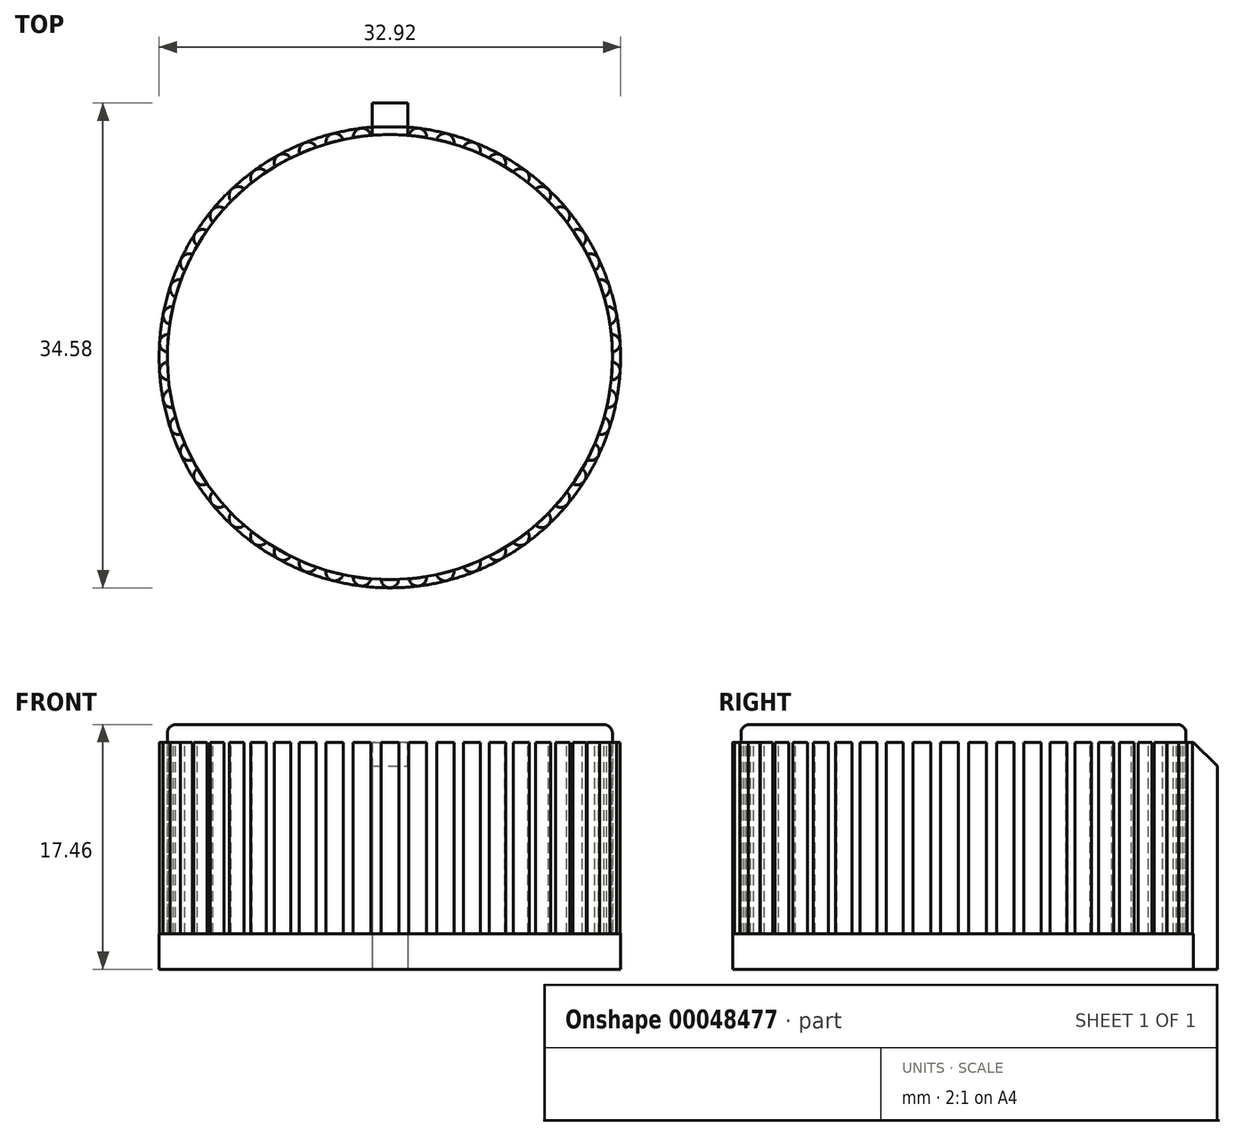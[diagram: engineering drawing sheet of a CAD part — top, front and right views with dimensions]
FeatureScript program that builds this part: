
annotation { "Feature Type Name" : "Feature", "Feature Type Description" : "" }
export const myFeature = defineFeature(function(context is Context, id is Id, definition is map)
    precondition{}
    {
        {
            var Q0;
            Q0=qCreatedBy(makeId("Top.planeOp"),FACE);
            var sketch = newSketch(context, id + "F0", { "sketchPlane" : qUnion([Q0])});
            skArc(sketch, "E0", {"start": v(-1.27, 15.82) * mm, "mid": v(0, -15.88) * mm, "end": v(1.27, 15.82) * mm});
            skLineSegment(sketch, "E1", {"start": v(0, 15.88) * mm, "end": v(0, -19.27) * mm, "construction": true});
            skLineSegment(sketch, "E2.rect.bottom", {"start": v(-1.27, 18.12) * mm, "end": v(1.27, 18.12) * mm});
            skLineSegment(sketch, "E2.rect.left", {"start": v(-1.27, 18.12) * mm, "end": v(-1.27, 15.82) * mm});
            skLineSegment(sketch, "E2.rect.right", {"start": v(1.27, 18.12) * mm, "end": v(1.27, 15.82) * mm});
            skPoint(sketch, "E2.rect.middle", {"position": v(0, 15.88) * mm});
            skPoint(sketch, "E3.orphan", {"position": v(-1.27, 13.63) * mm});
            skPoint(sketch, "E4.orphan", {"position": v(1.27, 13.63) * mm});
            skSolve(sketch);
        }
        {
            var Q0;
            Q0=makeQuery(id+"F0.imprint","IMPRINT",FACE,{"disambiguationData":[TD([[makeQuery(id+"F0.imprint","IMPRINT",EDGE,{"derivedFrom":sQuery(id+"F0.wireOp",EDGE,"E0")}),1.0]])]});
            extrude(context, id + "F1", {"entities" : qUnion([Q0]), "depth" : 17.46 * mm});
        }
        {
            var Q0;
            Q0=qCreatedBy(makeId("Front.planeOp"),FACE);
            cPlane(context, id + "F2", {"entities" : qUnion([Q0]), "cplaneType" : CPlaneType.OFFSET, "offset" : 15.88 * mm, "oppositeDirection" : true, "width" : 152.4 * mm, "height" : 152.4 * mm});
        }
        {
            var Q0;
            Q0=makeQuery(id+"F1.opExtrude","CAP_FACE",FACE,{"disambiguationData":[OSD([sQuery(id+"F0.wireOp",EDGE,"E0"),sQuery(id+"F0.wireOp",EDGE,"E2.rect.bottom"),sQuery(id+"F0.wireOp",EDGE,"E2.rect.left"),sQuery(id+"F0.wireOp",EDGE,"E2.rect.right")])],"isStart":false});
            var sketch = newSketch(context, id + "F3", { "sketchPlane" : qUnion([Q0])});
            skPoint(sketch, "E5", {"position": v(0, 0) * mm});
            skLineSegment(sketch, "E6", {"start": v(0, 0) * mm, "end": v(0, 15.88) * mm, "construction": true});
            skPoint(sketch, "E6.endSnap0", {"position": v(0, 18.12) * mm});
            skLineSegment(sketch, "E7", {"start": v(-1.27, 15.82) * mm, "end": v(1.27, 15.82) * mm, "construction": true});
            skCircle(sketch, "E8", {"center": v(0, 15.82) * mm, "radius": 0.64 * mm});
            skLineSegment(sketch, "E9.1.0", {"start": v(-13.07, -9.01) * mm, "end": v(-14.34, -6.81) * mm, "construction": true});
            skLineSegment(sketch, "E9.2.0", {"start": v(14.34, -6.81) * mm, "end": v(13.07, -9.01) * mm, "construction": true});
            skCircle(sketch, "E10.1.0", {"center": v(-1.98, 15.7) * mm, "radius": 0.64 * mm});
            skCircle(sketch, "E10.2.0", {"center": v(-3.94, 15.33) * mm, "radius": 0.64 * mm});
            skCircle(sketch, "E10.3.0", {"center": v(-5.83, 14.71) * mm, "radius": 0.64 * mm});
            skCircle(sketch, "E10.4.0", {"center": v(-7.62, 13.87) * mm, "radius": 0.64 * mm});
            skCircle(sketch, "E10.5.0", {"center": v(-9.3, 12.8) * mm, "radius": 0.64 * mm});
            skCircle(sketch, "E10.6.0", {"center": v(-10.83, 11.54) * mm, "radius": 0.64 * mm});
            skCircle(sketch, "E10.7.0", {"center": v(-12.2, 10.09) * mm, "radius": 0.64 * mm});
            skCircle(sketch, "E10.8.0", {"center": v(-13.36, 8.48) * mm, "radius": 0.64 * mm});
            skCircle(sketch, "E10.9.0", {"center": v(-14.32, 6.74) * mm, "radius": 0.64 * mm});
            skCircle(sketch, "E10.10.0", {"center": v(-15.05, 4.89) * mm, "radius": 0.64 * mm});
            skCircle(sketch, "E10.11.0", {"center": v(-15.54, 2.97) * mm, "radius": 0.64 * mm});
            skCircle(sketch, "E10.12.0", {"center": v(-15.8, 1) * mm, "radius": 0.64 * mm});
            skCircle(sketch, "E10.13.0", {"center": v(-15.8, -1) * mm, "radius": 0.64 * mm});
            skCircle(sketch, "E10.14.0", {"center": v(-15.54, -2.97) * mm, "radius": 0.64 * mm});
            skCircle(sketch, "E10.15.0", {"center": v(-15.05, -4.89) * mm, "radius": 0.64 * mm});
            skCircle(sketch, "E10.16.0", {"center": v(-14.32, -6.74) * mm, "radius": 0.64 * mm});
            skCircle(sketch, "E10.17.0", {"center": v(-13.36, -8.48) * mm, "radius": 0.64 * mm});
            skCircle(sketch, "E10.18.0", {"center": v(-12.2, -10.09) * mm, "radius": 0.64 * mm});
            skCircle(sketch, "E10.19.0", {"center": v(-10.83, -11.54) * mm, "radius": 0.64 * mm});
            skCircle(sketch, "E10.20.0", {"center": v(-9.3, -12.8) * mm, "radius": 0.64 * mm});
            skCircle(sketch, "E10.21.0", {"center": v(-7.62, -13.87) * mm, "radius": 0.64 * mm});
            skCircle(sketch, "E10.22.0", {"center": v(-5.83, -14.71) * mm, "radius": 0.64 * mm});
            skCircle(sketch, "E10.23.0", {"center": v(-3.94, -15.33) * mm, "radius": 0.64 * mm});
            skCircle(sketch, "E10.24.0", {"center": v(-1.98, -15.7) * mm, "radius": 0.64 * mm});
            skCircle(sketch, "E10.25.0", {"center": v(0, -15.82) * mm, "radius": 0.64 * mm});
            skCircle(sketch, "E10.26.0", {"center": v(1.98, -15.7) * mm, "radius": 0.64 * mm});
            skCircle(sketch, "E10.27.0", {"center": v(3.94, -15.33) * mm, "radius": 0.64 * mm});
            skCircle(sketch, "E10.28.0", {"center": v(5.83, -14.71) * mm, "radius": 0.64 * mm});
            skCircle(sketch, "E10.29.0", {"center": v(7.62, -13.87) * mm, "radius": 0.64 * mm});
            skCircle(sketch, "E10.30.0", {"center": v(9.3, -12.8) * mm, "radius": 0.64 * mm});
            skCircle(sketch, "E10.31.0", {"center": v(10.83, -11.54) * mm, "radius": 0.64 * mm});
            skCircle(sketch, "E10.32.0", {"center": v(12.2, -10.09) * mm, "radius": 0.64 * mm});
            skCircle(sketch, "E10.33.0", {"center": v(13.36, -8.48) * mm, "radius": 0.64 * mm});
            skCircle(sketch, "E10.34.0", {"center": v(14.32, -6.74) * mm, "radius": 0.64 * mm});
            skCircle(sketch, "E10.35.0", {"center": v(15.05, -4.89) * mm, "radius": 0.64 * mm});
            skCircle(sketch, "E10.36.0", {"center": v(15.54, -2.97) * mm, "radius": 0.64 * mm});
            skCircle(sketch, "E10.37.0", {"center": v(15.8, -1) * mm, "radius": 0.64 * mm});
            skCircle(sketch, "E10.38.0", {"center": v(15.8, 1) * mm, "radius": 0.64 * mm});
            skCircle(sketch, "E10.39.0", {"center": v(15.54, 2.97) * mm, "radius": 0.64 * mm});
            skCircle(sketch, "E11.1.40.0", {"center": v(15.05, 4.89) * mm, "radius": 0.64 * mm});
            skCircle(sketch, "E11.1.41.0", {"center": v(14.32, 6.74) * mm, "radius": 0.64 * mm});
            skCircle(sketch, "E11.1.42.0", {"center": v(13.36, 8.48) * mm, "radius": 0.64 * mm});
            skCircle(sketch, "E11.1.43.0", {"center": v(12.2, 10.09) * mm, "radius": 0.64 * mm});
            skCircle(sketch, "E11.1.44.0", {"center": v(10.83, 11.54) * mm, "radius": 0.64 * mm});
            skCircle(sketch, "E11.1.45.0", {"center": v(9.3, 12.8) * mm, "radius": 0.64 * mm});
            skCircle(sketch, "E11.1.46.0", {"center": v(7.62, 13.87) * mm, "radius": 0.64 * mm});
            skCircle(sketch, "E11.1.47.0", {"center": v(5.83, 14.71) * mm, "radius": 0.64 * mm});
            skCircle(sketch, "E11.1.48.0", {"center": v(3.94, 15.33) * mm, "radius": 0.64 * mm});
            skCircle(sketch, "E11.1.49.0", {"center": v(1.98, 15.7) * mm, "radius": 0.64 * mm});
            skSolve(sketch);
        }
        {
            var Q0;
            Q0 = qSketchRegion(id + "F3", true);
            var Q1;
            Q1=makeQuery(id+"F1.opExtrude","CAP_FACE",FACE,{"disambiguationData":[OSD([sQuery(id+"F0.wireOp",EDGE,"E0"),sQuery(id+"F0.wireOp",EDGE,"E2.rect.bottom"),sQuery(id+"F0.wireOp",EDGE,"E2.rect.left"),sQuery(id+"F0.wireOp",EDGE,"E2.rect.right")])],"isStart":true});
            extrude(context, id + "F4", {"entities" : qUnion([Q0]), "operationType" : NewBodyOperationType.ADD, "endBound" : BoundingType.UP_TO_SURFACE, "oppositeDirection" : true, "endBoundEntityFace" : qUnion([Q1]), "depth" : 25.4 * mm});
        }
        {
            var Q0;
            Q0=makeQuery(id+"F4.boolean.opBoolean","MERGE",FACE,{"derivedFrom":[makeQuery(id+"F1.opExtrude","CAP_FACE",FACE,{"disambiguationData":[OSD([sQuery(id+"F0.wireOp",EDGE,"E0"),sQuery(id+"F0.wireOp",EDGE,"E2.rect.bottom"),sQuery(id+"F0.wireOp",EDGE,"E2.rect.left"),sQuery(id+"F0.wireOp",EDGE,"E2.rect.right")])],"isStart":true}),makeQuery(id+"F4.opExtrude","CAP_FACE",FACE,{"disambiguationData":[OSD([sQuery(id+"F3.wireOp",EDGE,"E10.1.0")])],"isStart":false}),makeQuery(id+"F4.opExtrude","CAP_FACE",FACE,{"disambiguationData":[OSD([sQuery(id+"F3.wireOp",EDGE,"E10.2.0")])],"isStart":false}),makeQuery(id+"F4.opExtrude","CAP_FACE",FACE,{"disambiguationData":[OSD([sQuery(id+"F3.wireOp",EDGE,"E10.3.0")])],"isStart":false}),makeQuery(id+"F4.opExtrude","CAP_FACE",FACE,{"disambiguationData":[OSD([sQuery(id+"F3.wireOp",EDGE,"E10.4.0")])],"isStart":false}),makeQuery(id+"F4.opExtrude","CAP_FACE",FACE,{"disambiguationData":[OSD([sQuery(id+"F3.wireOp",EDGE,"E10.5.0")])],"isStart":false}),makeQuery(id+"F4.opExtrude","CAP_FACE",FACE,{"disambiguationData":[OSD([sQuery(id+"F3.wireOp",EDGE,"E10.6.0")])],"isStart":false}),makeQuery(id+"F4.opExtrude","CAP_FACE",FACE,{"disambiguationData":[OSD([sQuery(id+"F3.wireOp",EDGE,"E10.7.0")])],"isStart":false}),makeQuery(id+"F4.opExtrude","CAP_FACE",FACE,{"disambiguationData":[OSD([sQuery(id+"F3.wireOp",EDGE,"E10.8.0")])],"isStart":false}),makeQuery(id+"F4.opExtrude","CAP_FACE",FACE,{"disambiguationData":[OSD([sQuery(id+"F3.wireOp",EDGE,"E10.9.0")])],"isStart":false}),makeQuery(id+"F4.opExtrude","CAP_FACE",FACE,{"disambiguationData":[OSD([sQuery(id+"F3.wireOp",EDGE,"E10.10.0")])],"isStart":false}),makeQuery(id+"F4.opExtrude","CAP_FACE",FACE,{"disambiguationData":[OSD([sQuery(id+"F3.wireOp",EDGE,"E10.11.0")])],"isStart":false}),makeQuery(id+"F4.opExtrude","CAP_FACE",FACE,{"disambiguationData":[OSD([sQuery(id+"F3.wireOp",EDGE,"E10.12.0")])],"isStart":false}),makeQuery(id+"F4.opExtrude","CAP_FACE",FACE,{"disambiguationData":[OSD([sQuery(id+"F3.wireOp",EDGE,"E10.13.0")])],"isStart":false}),makeQuery(id+"F4.opExtrude","CAP_FACE",FACE,{"disambiguationData":[OSD([sQuery(id+"F3.wireOp",EDGE,"E10.14.0")])],"isStart":false}),makeQuery(id+"F4.opExtrude","CAP_FACE",FACE,{"disambiguationData":[OSD([sQuery(id+"F3.wireOp",EDGE,"E10.15.0")])],"isStart":false}),makeQuery(id+"F4.opExtrude","CAP_FACE",FACE,{"disambiguationData":[OSD([sQuery(id+"F3.wireOp",EDGE,"E10.16.0")])],"isStart":false}),makeQuery(id+"F4.opExtrude","CAP_FACE",FACE,{"disambiguationData":[OSD([sQuery(id+"F3.wireOp",EDGE,"E10.17.0")])],"isStart":false}),makeQuery(id+"F4.opExtrude","CAP_FACE",FACE,{"disambiguationData":[OSD([sQuery(id+"F3.wireOp",EDGE,"E10.18.0")])],"isStart":false}),makeQuery(id+"F4.opExtrude","CAP_FACE",FACE,{"disambiguationData":[OSD([sQuery(id+"F3.wireOp",EDGE,"E10.19.0")])],"isStart":false}),makeQuery(id+"F4.opExtrude","CAP_FACE",FACE,{"disambiguationData":[OSD([sQuery(id+"F3.wireOp",EDGE,"E10.20.0")])],"isStart":false}),makeQuery(id+"F4.opExtrude","CAP_FACE",FACE,{"disambiguationData":[OSD([sQuery(id+"F3.wireOp",EDGE,"E10.21.0")])],"isStart":false}),makeQuery(id+"F4.opExtrude","CAP_FACE",FACE,{"disambiguationData":[OSD([sQuery(id+"F3.wireOp",EDGE,"E10.22.0")])],"isStart":false}),makeQuery(id+"F4.opExtrude","CAP_FACE",FACE,{"disambiguationData":[OSD([sQuery(id+"F3.wireOp",EDGE,"E10.23.0")])],"isStart":false}),makeQuery(id+"F4.opExtrude","CAP_FACE",FACE,{"disambiguationData":[OSD([sQuery(id+"F3.wireOp",EDGE,"E10.24.0")])],"isStart":false}),makeQuery(id+"F4.opExtrude","CAP_FACE",FACE,{"disambiguationData":[OSD([sQuery(id+"F3.wireOp",EDGE,"E10.25.0")])],"isStart":false}),makeQuery(id+"F4.opExtrude","CAP_FACE",FACE,{"disambiguationData":[OSD([sQuery(id+"F3.wireOp",EDGE,"E10.26.0")])],"isStart":false}),makeQuery(id+"F4.opExtrude","CAP_FACE",FACE,{"disambiguationData":[OSD([sQuery(id+"F3.wireOp",EDGE,"E10.27.0")])],"isStart":false}),makeQuery(id+"F4.opExtrude","CAP_FACE",FACE,{"disambiguationData":[OSD([sQuery(id+"F3.wireOp",EDGE,"E10.28.0")])],"isStart":false}),makeQuery(id+"F4.opExtrude","CAP_FACE",FACE,{"disambiguationData":[OSD([sQuery(id+"F3.wireOp",EDGE,"E10.29.0")])],"isStart":false}),makeQuery(id+"F4.opExtrude","CAP_FACE",FACE,{"disambiguationData":[OSD([sQuery(id+"F3.wireOp",EDGE,"E10.30.0")])],"isStart":false}),makeQuery(id+"F4.opExtrude","CAP_FACE",FACE,{"disambiguationData":[OSD([sQuery(id+"F3.wireOp",EDGE,"E10.31.0")])],"isStart":false}),makeQuery(id+"F4.opExtrude","CAP_FACE",FACE,{"disambiguationData":[OSD([sQuery(id+"F3.wireOp",EDGE,"E10.32.0")])],"isStart":false}),makeQuery(id+"F4.opExtrude","CAP_FACE",FACE,{"disambiguationData":[OSD([sQuery(id+"F3.wireOp",EDGE,"E10.33.0")])],"isStart":false}),makeQuery(id+"F4.opExtrude","CAP_FACE",FACE,{"disambiguationData":[OSD([sQuery(id+"F3.wireOp",EDGE,"E10.34.0")])],"isStart":false}),makeQuery(id+"F4.opExtrude","CAP_FACE",FACE,{"disambiguationData":[OSD([sQuery(id+"F3.wireOp",EDGE,"E10.35.0")])],"isStart":false}),makeQuery(id+"F4.opExtrude","CAP_FACE",FACE,{"disambiguationData":[OSD([sQuery(id+"F3.wireOp",EDGE,"E10.36.0")])],"isStart":false}),makeQuery(id+"F4.opExtrude","CAP_FACE",FACE,{"disambiguationData":[OSD([sQuery(id+"F3.wireOp",EDGE,"E10.37.0")])],"isStart":false}),makeQuery(id+"F4.opExtrude","CAP_FACE",FACE,{"disambiguationData":[OSD([sQuery(id+"F3.wireOp",EDGE,"E10.38.0")])],"isStart":false}),makeQuery(id+"F4.opExtrude","CAP_FACE",FACE,{"disambiguationData":[OSD([sQuery(id+"F3.wireOp",EDGE,"E10.39.0")])],"isStart":false}),makeQuery(id+"F4.opExtrude","CAP_FACE",FACE,{"disambiguationData":[OSD([sQuery(id+"F3.wireOp",EDGE,"E11.1.40.0")])],"isStart":false}),makeQuery(id+"F4.opExtrude","CAP_FACE",FACE,{"disambiguationData":[OSD([sQuery(id+"F3.wireOp",EDGE,"E11.1.41.0")])],"isStart":false}),makeQuery(id+"F4.opExtrude","CAP_FACE",FACE,{"disambiguationData":[OSD([sQuery(id+"F3.wireOp",EDGE,"E11.1.42.0")])],"isStart":false}),makeQuery(id+"F4.opExtrude","CAP_FACE",FACE,{"disambiguationData":[OSD([sQuery(id+"F3.wireOp",EDGE,"E11.1.43.0")])],"isStart":false}),makeQuery(id+"F4.opExtrude","CAP_FACE",FACE,{"disambiguationData":[OSD([sQuery(id+"F3.wireOp",EDGE,"E11.1.44.0")])],"isStart":false}),makeQuery(id+"F4.opExtrude","CAP_FACE",FACE,{"disambiguationData":[OSD([sQuery(id+"F3.wireOp",EDGE,"E11.1.45.0")])],"isStart":false}),makeQuery(id+"F4.opExtrude","CAP_FACE",FACE,{"disambiguationData":[OSD([sQuery(id+"F3.wireOp",EDGE,"E11.1.46.0")])],"isStart":false}),makeQuery(id+"F4.opExtrude","CAP_FACE",FACE,{"disambiguationData":[OSD([sQuery(id+"F3.wireOp",EDGE,"E11.1.47.0")])],"isStart":false}),makeQuery(id+"F4.opExtrude","CAP_FACE",FACE,{"disambiguationData":[OSD([sQuery(id+"F3.wireOp",EDGE,"E11.1.48.0")])],"isStart":false}),makeQuery(id+"F4.opExtrude","CAP_FACE",FACE,{"disambiguationData":[OSD([sQuery(id+"F3.wireOp",EDGE,"E11.1.49.0")])],"isStart":false})]});
            var sketch = newSketch(context, id + "F5", { "sketchPlane" : qUnion([Q0])});
            skCircle(sketch, "E12", {"center": v(0, 0) * mm, "radius": 16.46 * mm});
            skSolve(sketch);
        }
        {
            var Q0;
            Q0 = qSketchRegion(id + "F5", true);
            extrude(context, id + "F6", {"entities" : qUnion([Q0]), "operationType" : NewBodyOperationType.ADD, "oppositeDirection" : true, "depth" : 2.54 * mm});
        }
        {
            var Q0;
            Q0=makeQuery(id+"F4.boolean.opBoolean","MERGE",FACE,{"derivedFrom":[makeQuery(id+"F1.opExtrude","CAP_FACE",FACE,{"disambiguationData":[OSD([sQuery(id+"F0.wireOp",EDGE,"E0"),sQuery(id+"F0.wireOp",EDGE,"E2.rect.bottom"),sQuery(id+"F0.wireOp",EDGE,"E2.rect.left"),sQuery(id+"F0.wireOp",EDGE,"E2.rect.right")])],"isStart":false}),makeQuery(id+"F4.opExtrude","CAP_FACE",FACE,{"disambiguationData":[OSD([sQuery(id+"F3.wireOp",EDGE,"E10.1.0")])],"isStart":true}),makeQuery(id+"F4.opExtrude","CAP_FACE",FACE,{"disambiguationData":[OSD([sQuery(id+"F3.wireOp",EDGE,"E10.2.0")])],"isStart":true}),makeQuery(id+"F4.opExtrude","CAP_FACE",FACE,{"disambiguationData":[OSD([sQuery(id+"F3.wireOp",EDGE,"E10.3.0")])],"isStart":true}),makeQuery(id+"F4.opExtrude","CAP_FACE",FACE,{"disambiguationData":[OSD([sQuery(id+"F3.wireOp",EDGE,"E10.4.0")])],"isStart":true}),makeQuery(id+"F4.opExtrude","CAP_FACE",FACE,{"disambiguationData":[OSD([sQuery(id+"F3.wireOp",EDGE,"E10.5.0")])],"isStart":true}),makeQuery(id+"F4.opExtrude","CAP_FACE",FACE,{"disambiguationData":[OSD([sQuery(id+"F3.wireOp",EDGE,"E10.6.0")])],"isStart":true}),makeQuery(id+"F4.opExtrude","CAP_FACE",FACE,{"disambiguationData":[OSD([sQuery(id+"F3.wireOp",EDGE,"E10.7.0")])],"isStart":true}),makeQuery(id+"F4.opExtrude","CAP_FACE",FACE,{"disambiguationData":[OSD([sQuery(id+"F3.wireOp",EDGE,"E10.8.0")])],"isStart":true}),makeQuery(id+"F4.opExtrude","CAP_FACE",FACE,{"disambiguationData":[OSD([sQuery(id+"F3.wireOp",EDGE,"E10.9.0")])],"isStart":true}),makeQuery(id+"F4.opExtrude","CAP_FACE",FACE,{"disambiguationData":[OSD([sQuery(id+"F3.wireOp",EDGE,"E10.10.0")])],"isStart":true}),makeQuery(id+"F4.opExtrude","CAP_FACE",FACE,{"disambiguationData":[OSD([sQuery(id+"F3.wireOp",EDGE,"E10.11.0")])],"isStart":true}),makeQuery(id+"F4.opExtrude","CAP_FACE",FACE,{"disambiguationData":[OSD([sQuery(id+"F3.wireOp",EDGE,"E10.12.0")])],"isStart":true}),makeQuery(id+"F4.opExtrude","CAP_FACE",FACE,{"disambiguationData":[OSD([sQuery(id+"F3.wireOp",EDGE,"E10.13.0")])],"isStart":true}),makeQuery(id+"F4.opExtrude","CAP_FACE",FACE,{"disambiguationData":[OSD([sQuery(id+"F3.wireOp",EDGE,"E10.14.0")])],"isStart":true}),makeQuery(id+"F4.opExtrude","CAP_FACE",FACE,{"disambiguationData":[OSD([sQuery(id+"F3.wireOp",EDGE,"E10.15.0")])],"isStart":true}),makeQuery(id+"F4.opExtrude","CAP_FACE",FACE,{"disambiguationData":[OSD([sQuery(id+"F3.wireOp",EDGE,"E10.16.0")])],"isStart":true}),makeQuery(id+"F4.opExtrude","CAP_FACE",FACE,{"disambiguationData":[OSD([sQuery(id+"F3.wireOp",EDGE,"E10.17.0")])],"isStart":true}),makeQuery(id+"F4.opExtrude","CAP_FACE",FACE,{"disambiguationData":[OSD([sQuery(id+"F3.wireOp",EDGE,"E10.18.0")])],"isStart":true}),makeQuery(id+"F4.opExtrude","CAP_FACE",FACE,{"disambiguationData":[OSD([sQuery(id+"F3.wireOp",EDGE,"E10.19.0")])],"isStart":true}),makeQuery(id+"F4.opExtrude","CAP_FACE",FACE,{"disambiguationData":[OSD([sQuery(id+"F3.wireOp",EDGE,"E10.20.0")])],"isStart":true}),makeQuery(id+"F4.opExtrude","CAP_FACE",FACE,{"disambiguationData":[OSD([sQuery(id+"F3.wireOp",EDGE,"E10.21.0")])],"isStart":true}),makeQuery(id+"F4.opExtrude","CAP_FACE",FACE,{"disambiguationData":[OSD([sQuery(id+"F3.wireOp",EDGE,"E10.22.0")])],"isStart":true}),makeQuery(id+"F4.opExtrude","CAP_FACE",FACE,{"disambiguationData":[OSD([sQuery(id+"F3.wireOp",EDGE,"E10.23.0")])],"isStart":true}),makeQuery(id+"F4.opExtrude","CAP_FACE",FACE,{"disambiguationData":[OSD([sQuery(id+"F3.wireOp",EDGE,"E10.24.0")])],"isStart":true}),makeQuery(id+"F4.opExtrude","CAP_FACE",FACE,{"disambiguationData":[OSD([sQuery(id+"F3.wireOp",EDGE,"E10.25.0")])],"isStart":true}),makeQuery(id+"F4.opExtrude","CAP_FACE",FACE,{"disambiguationData":[OSD([sQuery(id+"F3.wireOp",EDGE,"E10.26.0")])],"isStart":true}),makeQuery(id+"F4.opExtrude","CAP_FACE",FACE,{"disambiguationData":[OSD([sQuery(id+"F3.wireOp",EDGE,"E10.27.0")])],"isStart":true}),makeQuery(id+"F4.opExtrude","CAP_FACE",FACE,{"disambiguationData":[OSD([sQuery(id+"F3.wireOp",EDGE,"E10.28.0")])],"isStart":true}),makeQuery(id+"F4.opExtrude","CAP_FACE",FACE,{"disambiguationData":[OSD([sQuery(id+"F3.wireOp",EDGE,"E10.29.0")])],"isStart":true}),makeQuery(id+"F4.opExtrude","CAP_FACE",FACE,{"disambiguationData":[OSD([sQuery(id+"F3.wireOp",EDGE,"E10.30.0")])],"isStart":true}),makeQuery(id+"F4.opExtrude","CAP_FACE",FACE,{"disambiguationData":[OSD([sQuery(id+"F3.wireOp",EDGE,"E10.31.0")])],"isStart":true}),makeQuery(id+"F4.opExtrude","CAP_FACE",FACE,{"disambiguationData":[OSD([sQuery(id+"F3.wireOp",EDGE,"E10.32.0")])],"isStart":true}),makeQuery(id+"F4.opExtrude","CAP_FACE",FACE,{"disambiguationData":[OSD([sQuery(id+"F3.wireOp",EDGE,"E10.33.0")])],"isStart":true}),makeQuery(id+"F4.opExtrude","CAP_FACE",FACE,{"disambiguationData":[OSD([sQuery(id+"F3.wireOp",EDGE,"E10.34.0")])],"isStart":true}),makeQuery(id+"F4.opExtrude","CAP_FACE",FACE,{"disambiguationData":[OSD([sQuery(id+"F3.wireOp",EDGE,"E10.35.0")])],"isStart":true}),makeQuery(id+"F4.opExtrude","CAP_FACE",FACE,{"disambiguationData":[OSD([sQuery(id+"F3.wireOp",EDGE,"E10.36.0")])],"isStart":true}),makeQuery(id+"F4.opExtrude","CAP_FACE",FACE,{"disambiguationData":[OSD([sQuery(id+"F3.wireOp",EDGE,"E10.37.0")])],"isStart":true}),makeQuery(id+"F4.opExtrude","CAP_FACE",FACE,{"disambiguationData":[OSD([sQuery(id+"F3.wireOp",EDGE,"E10.38.0")])],"isStart":true}),makeQuery(id+"F4.opExtrude","CAP_FACE",FACE,{"disambiguationData":[OSD([sQuery(id+"F3.wireOp",EDGE,"E10.39.0")])],"isStart":true}),makeQuery(id+"F4.opExtrude","CAP_FACE",FACE,{"disambiguationData":[OSD([sQuery(id+"F3.wireOp",EDGE,"E11.1.40.0")])],"isStart":true}),makeQuery(id+"F4.opExtrude","CAP_FACE",FACE,{"disambiguationData":[OSD([sQuery(id+"F3.wireOp",EDGE,"E11.1.41.0")])],"isStart":true}),makeQuery(id+"F4.opExtrude","CAP_FACE",FACE,{"disambiguationData":[OSD([sQuery(id+"F3.wireOp",EDGE,"E11.1.42.0")])],"isStart":true}),makeQuery(id+"F4.opExtrude","CAP_FACE",FACE,{"disambiguationData":[OSD([sQuery(id+"F3.wireOp",EDGE,"E11.1.43.0")])],"isStart":true}),makeQuery(id+"F4.opExtrude","CAP_FACE",FACE,{"disambiguationData":[OSD([sQuery(id+"F3.wireOp",EDGE,"E11.1.44.0")])],"isStart":true}),makeQuery(id+"F4.opExtrude","CAP_FACE",FACE,{"disambiguationData":[OSD([sQuery(id+"F3.wireOp",EDGE,"E11.1.45.0")])],"isStart":true}),makeQuery(id+"F4.opExtrude","CAP_FACE",FACE,{"disambiguationData":[OSD([sQuery(id+"F3.wireOp",EDGE,"E11.1.46.0")])],"isStart":true}),makeQuery(id+"F4.opExtrude","CAP_FACE",FACE,{"disambiguationData":[OSD([sQuery(id+"F3.wireOp",EDGE,"E11.1.47.0")])],"isStart":true}),makeQuery(id+"F4.opExtrude","CAP_FACE",FACE,{"disambiguationData":[OSD([sQuery(id+"F3.wireOp",EDGE,"E11.1.48.0")])],"isStart":true}),makeQuery(id+"F4.opExtrude","CAP_FACE",FACE,{"disambiguationData":[OSD([sQuery(id+"F3.wireOp",EDGE,"E11.1.49.0")])],"isStart":true})]});
            var sketch = newSketch(context, id + "F7", { "sketchPlane" : qUnion([Q0])});
            skCircle(sketch, "E13", {"center": v(0, 0) * mm, "radius": 16.46 * mm});
            skCircle(sketch, "E14", {"center": v(0, 0) * mm, "radius": 15.87 * mm});
            skSolve(sketch);
        }
        {
            var Q0;
            Q0 = qSketchRegion(id + "F7", true);
            extrude(context, id + "F8", {"entities" : qUnion([Q0]), "operationType" : NewBodyOperationType.REMOVE, "oppositeDirection" : true, "depth" : 1.27 * mm});
        }
        {
            var Q0;
            {var subQ0=sQuery(id+"F0.wireOp",EDGE,"E0");var subQ1=makeQuery(id+"F1.opExtrude","CAP_EDGE",EDGE,{"disambiguationData":[OSD([subQ0])],"isStart":false});var subQ2=sQuery(id+"F3.wireOp",EDGE,"E11.1.49.0");var subQ3=makeQuery(id+"F4.opExtrude","CAP_FACE",FACE,{"disambiguationData":[OSD([subQ2])],"isStart":true});var subQ4=sQuery(id+"F3.wireOp",EDGE,"E11.1.48.0");var subQ5=makeQuery(id+"F4.opExtrude","CAP_FACE",FACE,{"disambiguationData":[OSD([subQ4])],"isStart":true});var subQ6=sQuery(id+"F3.wireOp",EDGE,"E11.1.47.0");var subQ7=makeQuery(id+"F4.opExtrude","CAP_FACE",FACE,{"disambiguationData":[OSD([subQ6])],"isStart":true});var subQ8=sQuery(id+"F3.wireOp",EDGE,"E11.1.46.0");var subQ9=makeQuery(id+"F4.opExtrude","CAP_FACE",FACE,{"disambiguationData":[OSD([subQ8])],"isStart":true});var subQ10=sQuery(id+"F3.wireOp",EDGE,"E11.1.45.0");var subQ11=makeQuery(id+"F4.opExtrude","CAP_FACE",FACE,{"disambiguationData":[OSD([subQ10])],"isStart":true});var subQ12=sQuery(id+"F3.wireOp",EDGE,"E11.1.44.0");var subQ13=makeQuery(id+"F4.opExtrude","CAP_FACE",FACE,{"disambiguationData":[OSD([subQ12])],"isStart":true});var subQ14=sQuery(id+"F3.wireOp",EDGE,"E11.1.43.0");var subQ15=makeQuery(id+"F4.opExtrude","CAP_FACE",FACE,{"disambiguationData":[OSD([subQ14])],"isStart":true});var subQ16=sQuery(id+"F3.wireOp",EDGE,"E10.16.0");var subQ17=makeQuery(id+"F4.opExtrude","CAP_FACE",FACE,{"disambiguationData":[OSD([subQ16])],"isStart":true});var subQ18=sQuery(id+"F3.wireOp",EDGE,"E10.26.0");var subQ19=makeQuery(id+"F4.opExtrude","CAP_FACE",FACE,{"disambiguationData":[OSD([subQ18])],"isStart":true});var subQ20=sQuery(id+"F3.wireOp",EDGE,"E10.15.0");var subQ21=makeQuery(id+"F4.opExtrude","CAP_FACE",FACE,{"disambiguationData":[OSD([subQ20])],"isStart":true});var subQ22=sQuery(id+"F3.wireOp",EDGE,"E10.12.0");var subQ23=makeQuery(id+"F4.opExtrude","CAP_FACE",FACE,{"disambiguationData":[OSD([subQ22])],"isStart":true});var subQ24=sQuery(id+"F3.wireOp",EDGE,"E10.39.0");var subQ25=makeQuery(id+"F4.opExtrude","CAP_FACE",FACE,{"disambiguationData":[OSD([subQ24])],"isStart":true});var subQ26=sQuery(id+"F3.wireOp",EDGE,"E10.10.0");var subQ27=makeQuery(id+"F4.opExtrude","CAP_FACE",FACE,{"disambiguationData":[OSD([subQ26])],"isStart":true});var subQ28=sQuery(id+"F3.wireOp",EDGE,"E11.1.41.0");var subQ29=makeQuery(id+"F4.opExtrude","CAP_FACE",FACE,{"disambiguationData":[OSD([subQ28])],"isStart":true});var subQ30=sQuery(id+"F3.wireOp",EDGE,"E10.9.0");var subQ31=makeQuery(id+"F4.opExtrude","CAP_FACE",FACE,{"disambiguationData":[OSD([subQ30])],"isStart":true});var subQ32=sQuery(id+"F3.wireOp",EDGE,"E10.6.0");var subQ33=makeQuery(id+"F4.opExtrude","CAP_FACE",FACE,{"disambiguationData":[OSD([subQ32])],"isStart":true});var subQ34=sQuery(id+"F3.wireOp",EDGE,"E10.37.0");var subQ35=makeQuery(id+"F4.opExtrude","CAP_FACE",FACE,{"disambiguationData":[OSD([subQ34])],"isStart":true});var subQ36=sQuery(id+"F3.wireOp",EDGE,"E10.4.0");var subQ37=makeQuery(id+"F4.opExtrude","CAP_FACE",FACE,{"disambiguationData":[OSD([subQ36])],"isStart":true});var subQ38=sQuery(id+"F3.wireOp",EDGE,"E10.32.0");var subQ39=makeQuery(id+"F4.opExtrude","CAP_FACE",FACE,{"disambiguationData":[OSD([subQ38])],"isStart":true});var subQ40=sQuery(id+"F0.wireOp",EDGE,"E2.rect.left");var subQ41=sQuery(id+"F0.wireOp",EDGE,"E2.rect.right");var subQ42=makeQuery(id+"F1.opExtrude","CAP_FACE",FACE,{"disambiguationData":[OSD([subQ0,sQuery(id+"F0.wireOp",EDGE,"E2.rect.bottom"),subQ40,subQ41])],"isStart":false});var subQ43=sQuery(id+"F3.wireOp",EDGE,"E10.8.0");var subQ44=makeQuery(id+"F4.opExtrude","CAP_FACE",FACE,{"disambiguationData":[OSD([subQ43])],"isStart":true});var subQ45=sQuery(id+"F3.wireOp",EDGE,"E10.2.0");var subQ46=makeQuery(id+"F4.opExtrude","CAP_FACE",FACE,{"disambiguationData":[OSD([subQ45])],"isStart":true});var subQ47=sQuery(id+"F3.wireOp",EDGE,"E10.17.0");var subQ48=makeQuery(id+"F4.opExtrude","CAP_FACE",FACE,{"disambiguationData":[OSD([subQ47])],"isStart":true});var subQ49=makeQuery(id+"F1.opExtrude","SWEPT_FACE",FACE,{"disambiguationData":[OSD([subQ0])]});var subQ50=sQuery(id+"F3.wireOp",EDGE,"E10.13.0");var subQ51=makeQuery(id+"F4.opExtrude","CAP_FACE",FACE,{"disambiguationData":[OSD([subQ50])],"isStart":true});var subQ52=sQuery(id+"F3.wireOp",EDGE,"E10.5.0");var subQ53=makeQuery(id+"F4.opExtrude","CAP_FACE",FACE,{"disambiguationData":[OSD([subQ52])],"isStart":true});var subQ54=sQuery(id+"F3.wireOp",EDGE,"E10.7.0");var subQ55=makeQuery(id+"F4.opExtrude","CAP_FACE",FACE,{"disambiguationData":[OSD([subQ54])],"isStart":true});var subQ56=sQuery(id+"F3.wireOp",EDGE,"E10.3.0");var subQ57=makeQuery(id+"F4.opExtrude","CAP_FACE",FACE,{"disambiguationData":[OSD([subQ56])],"isStart":true});var subQ58=sQuery(id+"F3.wireOp",EDGE,"E10.18.0");var subQ59=makeQuery(id+"F4.opExtrude","CAP_FACE",FACE,{"disambiguationData":[OSD([subQ58])],"isStart":true});var subQ60=sQuery(id+"F3.wireOp",EDGE,"E10.1.0");var subQ61=makeQuery(id+"F4.opExtrude","CAP_FACE",FACE,{"disambiguationData":[OSD([subQ60])],"isStart":true});var subQ62=sQuery(id+"F3.wireOp",EDGE,"E10.19.0");var subQ63=makeQuery(id+"F4.opExtrude","CAP_FACE",FACE,{"disambiguationData":[OSD([subQ62])],"isStart":true});var subQ64=sQuery(id+"F3.wireOp",EDGE,"E10.20.0");var subQ65=makeQuery(id+"F4.opExtrude","CAP_FACE",FACE,{"disambiguationData":[OSD([subQ64])],"isStart":true});var subQ66=sQuery(id+"F3.wireOp",EDGE,"E10.38.0");var subQ67=makeQuery(id+"F4.opExtrude","CAP_FACE",FACE,{"disambiguationData":[OSD([subQ66])],"isStart":true});var subQ68=sQuery(id+"F3.wireOp",EDGE,"E10.21.0");var subQ69=makeQuery(id+"F4.opExtrude","CAP_FACE",FACE,{"disambiguationData":[OSD([subQ68])],"isStart":true});var subQ70=sQuery(id+"F3.wireOp",EDGE,"E10.31.0");var subQ71=makeQuery(id+"F4.opExtrude","CAP_FACE",FACE,{"disambiguationData":[OSD([subQ70])],"isStart":true});var subQ72=sQuery(id+"F3.wireOp",EDGE,"E10.36.0");var subQ73=makeQuery(id+"F4.opExtrude","CAP_FACE",FACE,{"disambiguationData":[OSD([subQ72])],"isStart":true});var subQ74=sQuery(id+"F3.wireOp",EDGE,"E10.22.0");var subQ75=makeQuery(id+"F4.opExtrude","CAP_FACE",FACE,{"disambiguationData":[OSD([subQ74])],"isStart":true});var subQ76=sQuery(id+"F3.wireOp",EDGE,"E10.14.0");var subQ77=makeQuery(id+"F4.opExtrude","CAP_FACE",FACE,{"disambiguationData":[OSD([subQ76])],"isStart":true});var subQ78=sQuery(id+"F3.wireOp",EDGE,"E10.23.0");var subQ79=makeQuery(id+"F4.opExtrude","CAP_FACE",FACE,{"disambiguationData":[OSD([subQ78])],"isStart":true});var subQ80=sQuery(id+"F3.wireOp",EDGE,"E10.11.0");var subQ81=makeQuery(id+"F4.opExtrude","CAP_FACE",FACE,{"disambiguationData":[OSD([subQ80])],"isStart":true});var subQ82=sQuery(id+"F3.wireOp",EDGE,"E10.25.0");var subQ83=makeQuery(id+"F4.opExtrude","CAP_FACE",FACE,{"disambiguationData":[OSD([subQ82])],"isStart":true});var subQ84=sQuery(id+"F3.wireOp",EDGE,"E10.27.0");var subQ85=makeQuery(id+"F4.opExtrude","CAP_FACE",FACE,{"disambiguationData":[OSD([subQ84])],"isStart":true});var subQ86=sQuery(id+"F3.wireOp",EDGE,"E10.28.0");var subQ87=makeQuery(id+"F4.opExtrude","CAP_FACE",FACE,{"disambiguationData":[OSD([subQ86])],"isStart":true});var subQ88=makeQuery(id+"F4.opExtrude","SWEPT_FACE",FACE,{"disambiguationData":[OSD([subQ60])]});var subQ89=sQuery(id+"F3.wireOp",EDGE,"E10.29.0");var subQ90=makeQuery(id+"F4.opExtrude","CAP_FACE",FACE,{"disambiguationData":[OSD([subQ89])],"isStart":true});var subQ91=sQuery(id+"F3.wireOp",EDGE,"E10.30.0");var subQ92=makeQuery(id+"F4.opExtrude","CAP_FACE",FACE,{"disambiguationData":[OSD([subQ91])],"isStart":true});var subQ93=sQuery(id+"F3.wireOp",EDGE,"E10.24.0");var subQ94=makeQuery(id+"F4.opExtrude","CAP_FACE",FACE,{"disambiguationData":[OSD([subQ93])],"isStart":true});var subQ95=sQuery(id+"F3.wireOp",EDGE,"E10.33.0");var subQ96=makeQuery(id+"F4.opExtrude","CAP_FACE",FACE,{"disambiguationData":[OSD([subQ95])],"isStart":true});var subQ97=sQuery(id+"F3.wireOp",EDGE,"E10.34.0");var subQ98=makeQuery(id+"F4.opExtrude","CAP_FACE",FACE,{"disambiguationData":[OSD([subQ97])],"isStart":true});var subQ99=sQuery(id+"F3.wireOp",EDGE,"E10.35.0");var subQ100=makeQuery(id+"F4.opExtrude","CAP_FACE",FACE,{"disambiguationData":[OSD([subQ99])],"isStart":true});var subQ101=sQuery(id+"F3.wireOp",EDGE,"E11.1.40.0");var subQ102=makeQuery(id+"F4.opExtrude","CAP_FACE",FACE,{"disambiguationData":[OSD([subQ101])],"isStart":true});var subQ103=sQuery(id+"F3.wireOp",EDGE,"E11.1.42.0");var subQ104=makeQuery(id+"F4.opExtrude","CAP_FACE",FACE,{"disambiguationData":[OSD([subQ103])],"isStart":true});var subQ105=makeQuery(id+"F4.opExtrude","SWEPT_FACE",FACE,{"disambiguationData":[OSD([subQ2])]});var subQ106=makeQuery(id+"F4.opExtrude","SWEPT_FACE",FACE,{"disambiguationData":[OSD([subQ45])]});var subQ107=makeQuery(id+"F4.opExtrude","SWEPT_FACE",FACE,{"disambiguationData":[OSD([subQ56])]});var subQ108=makeQuery(id+"F4.opExtrude","SWEPT_FACE",FACE,{"disambiguationData":[OSD([subQ36])]});var subQ109=makeQuery(id+"F4.opExtrude","SWEPT_FACE",FACE,{"disambiguationData":[OSD([subQ52])]});var subQ110=makeQuery(id+"F4.opExtrude","SWEPT_FACE",FACE,{"disambiguationData":[OSD([subQ32])]});var subQ111=makeQuery(id+"F4.opExtrude","SWEPT_FACE",FACE,{"disambiguationData":[OSD([subQ54])]});var subQ112=makeQuery(id+"F4.opExtrude","SWEPT_FACE",FACE,{"disambiguationData":[OSD([subQ43])]});var subQ113=makeQuery(id+"F4.opExtrude","SWEPT_FACE",FACE,{"disambiguationData":[OSD([subQ30])]});var subQ114=makeQuery(id+"F4.opExtrude","SWEPT_FACE",FACE,{"disambiguationData":[OSD([subQ26])]});var subQ115=makeQuery(id+"F4.opExtrude","SWEPT_FACE",FACE,{"disambiguationData":[OSD([subQ80])]});var subQ116=makeQuery(id+"F4.opExtrude","SWEPT_FACE",FACE,{"disambiguationData":[OSD([subQ22])]});var subQ117=makeQuery(id+"F4.opExtrude","SWEPT_FACE",FACE,{"disambiguationData":[OSD([subQ50])]});var subQ118=makeQuery(id+"F4.opExtrude","SWEPT_FACE",FACE,{"disambiguationData":[OSD([subQ76])]});var subQ119=makeQuery(id+"F4.opExtrude","SWEPT_FACE",FACE,{"disambiguationData":[OSD([subQ20])]});var subQ120=makeQuery(id+"F4.opExtrude","SWEPT_FACE",FACE,{"disambiguationData":[OSD([subQ16])]});var subQ121=makeQuery(id+"F4.opExtrude","SWEPT_FACE",FACE,{"disambiguationData":[OSD([subQ47])]});var subQ122=makeQuery(id+"F4.opExtrude","SWEPT_FACE",FACE,{"disambiguationData":[OSD([subQ58])]});var subQ123=makeQuery(id+"F4.opExtrude","SWEPT_FACE",FACE,{"disambiguationData":[OSD([subQ62])]});var subQ124=makeQuery(id+"F4.opExtrude","SWEPT_FACE",FACE,{"disambiguationData":[OSD([subQ64])]});var subQ125=makeQuery(id+"F4.opExtrude","SWEPT_FACE",FACE,{"disambiguationData":[OSD([subQ68])]});var subQ126=makeQuery(id+"F4.opExtrude","SWEPT_FACE",FACE,{"disambiguationData":[OSD([subQ74])]});var subQ127=makeQuery(id+"F4.opExtrude","SWEPT_FACE",FACE,{"disambiguationData":[OSD([subQ78])]});var subQ128=makeQuery(id+"F4.opExtrude","SWEPT_FACE",FACE,{"disambiguationData":[OSD([subQ93])]});var subQ129=makeQuery(id+"F4.opExtrude","SWEPT_FACE",FACE,{"disambiguationData":[OSD([subQ82])]});var subQ130=makeQuery(id+"F4.opExtrude","SWEPT_FACE",FACE,{"disambiguationData":[OSD([subQ18])]});var subQ131=makeQuery(id+"F4.opExtrude","SWEPT_FACE",FACE,{"disambiguationData":[OSD([subQ84])]});var subQ132=makeQuery(id+"F4.opExtrude","SWEPT_FACE",FACE,{"disambiguationData":[OSD([subQ86])]});var subQ133=makeQuery(id+"F4.opExtrude","SWEPT_FACE",FACE,{"disambiguationData":[OSD([subQ89])]});var subQ134=makeQuery(id+"F4.opExtrude","SWEPT_FACE",FACE,{"disambiguationData":[OSD([subQ91])]});var subQ135=makeQuery(id+"F4.opExtrude","SWEPT_FACE",FACE,{"disambiguationData":[OSD([subQ70])]});var subQ136=makeQuery(id+"F4.opExtrude","SWEPT_FACE",FACE,{"disambiguationData":[OSD([subQ38])]});var subQ137=makeQuery(id+"F4.opExtrude","SWEPT_FACE",FACE,{"disambiguationData":[OSD([subQ95])]});var subQ138=makeQuery(id+"F4.opExtrude","SWEPT_FACE",FACE,{"disambiguationData":[OSD([subQ97])]});var subQ139=makeQuery(id+"F4.opExtrude","SWEPT_FACE",FACE,{"disambiguationData":[OSD([subQ99])]});var subQ140=makeQuery(id+"F4.opExtrude","SWEPT_FACE",FACE,{"disambiguationData":[OSD([subQ72])]});var subQ141=makeQuery(id+"F4.opExtrude","SWEPT_FACE",FACE,{"disambiguationData":[OSD([subQ34])]});var subQ142=makeQuery(id+"F4.opExtrude","SWEPT_FACE",FACE,{"disambiguationData":[OSD([subQ66])]});var subQ143=makeQuery(id+"F4.opExtrude","SWEPT_FACE",FACE,{"disambiguationData":[OSD([subQ24])]});var subQ144=makeQuery(id+"F4.opExtrude","SWEPT_FACE",FACE,{"disambiguationData":[OSD([subQ101])]});var subQ145=makeQuery(id+"F4.opExtrude","SWEPT_FACE",FACE,{"disambiguationData":[OSD([subQ28])]});var subQ146=makeQuery(id+"F4.opExtrude","SWEPT_FACE",FACE,{"disambiguationData":[OSD([subQ103])]});var subQ147=makeQuery(id+"F4.opExtrude","SWEPT_FACE",FACE,{"disambiguationData":[OSD([subQ14])]});var subQ148=makeQuery(id+"F4.opExtrude","SWEPT_FACE",FACE,{"disambiguationData":[OSD([subQ12])]});var subQ149=makeQuery(id+"F4.opExtrude","SWEPT_FACE",FACE,{"disambiguationData":[OSD([subQ10])]});var subQ150=makeQuery(id+"F4.opExtrude","SWEPT_FACE",FACE,{"disambiguationData":[OSD([subQ8])]});var subQ151=makeQuery(id+"F4.opExtrude","SWEPT_FACE",FACE,{"disambiguationData":[OSD([subQ6])]});var subQ152=makeQuery(id+"F4.opExtrude","SWEPT_FACE",FACE,{"disambiguationData":[OSD([subQ4])]});Q0=makeQuery(id+"F8.boolean.opBoolean","MERGE",EDGE,{"derivedFrom":[makeQuery(id+"F4.boolean.opBoolean","SPLIT",EDGE,{"disambiguationData":[TD([subQ49,subQ42,makeQuery(id+"F1.opExtrude","SWEPT_FACE",FACE,{"disambiguationData":[OSD([subQ40])]}),subQ88,subQ61,subQ46,subQ57,subQ37,subQ53,subQ33,subQ55,subQ44,subQ31,subQ27,subQ81,subQ23,subQ51,subQ77,subQ21,subQ17,subQ48,subQ59,subQ63,subQ65,subQ69,subQ75,subQ79,subQ94,subQ83,subQ19,subQ85,subQ87,subQ90,subQ92,subQ71,subQ39,subQ96,subQ98,subQ100,subQ73,subQ35,subQ67,subQ25,subQ102,subQ29,subQ104,subQ15,subQ13,subQ11,subQ9,subQ7,subQ5,subQ3])],"derivedFrom":subQ1}),makeQuery(id+"F4.boolean.opBoolean","SPLIT",EDGE,{"disambiguationData":[TD([subQ49,subQ42,makeQuery(id+"F1.opExtrude","SWEPT_FACE",FACE,{"disambiguationData":[OSD([subQ41])]}),subQ61,subQ46,subQ57,subQ37,subQ53,subQ33,subQ55,subQ44,subQ31,subQ27,subQ81,subQ23,subQ51,subQ77,subQ21,subQ17,subQ48,subQ59,subQ63,subQ65,subQ69,subQ75,subQ79,subQ94,subQ83,subQ19,subQ85,subQ87,subQ90,subQ92,subQ71,subQ39,subQ96,subQ98,subQ100,subQ73,subQ35,subQ67,subQ25,subQ102,subQ29,subQ104,subQ15,subQ13,subQ11,subQ9,subQ7,subQ5,subQ105,subQ3])],"derivedFrom":subQ1}),makeQuery(id+"F4.boolean.opBoolean","SPLIT",EDGE,{"disambiguationData":[TD([subQ49,subQ42,subQ88,subQ61,subQ106,subQ46,subQ57,subQ37,subQ53,subQ33,subQ55,subQ44,subQ31,subQ27,subQ81,subQ23,subQ51,subQ77,subQ21,subQ17,subQ48,subQ59,subQ63,subQ65,subQ69,subQ75,subQ79,subQ94,subQ83,subQ19,subQ85,subQ87,subQ90,subQ92,subQ71,subQ39,subQ96,subQ98,subQ100,subQ73,subQ35,subQ67,subQ25,subQ102,subQ29,subQ104,subQ15,subQ13,subQ11,subQ9,subQ7,subQ5,subQ3])],"derivedFrom":subQ1}),makeQuery(id+"F4.boolean.opBoolean","SPLIT",EDGE,{"disambiguationData":[TD([subQ49,subQ42,subQ61,subQ106,subQ46,subQ107,subQ57,subQ37,subQ53,subQ33,subQ55,subQ44,subQ31,subQ27,subQ81,subQ23,subQ51,subQ77,subQ21,subQ17,subQ48,subQ59,subQ63,subQ65,subQ69,subQ75,subQ79,subQ94,subQ83,subQ19,subQ85,subQ87,subQ90,subQ92,subQ71,subQ39,subQ96,subQ98,subQ100,subQ73,subQ35,subQ67,subQ25,subQ102,subQ29,subQ104,subQ15,subQ13,subQ11,subQ9,subQ7,subQ5,subQ3])],"derivedFrom":subQ1}),makeQuery(id+"F4.boolean.opBoolean","SPLIT",EDGE,{"disambiguationData":[TD([subQ49,subQ42,subQ61,subQ46,subQ107,subQ57,subQ108,subQ37,subQ53,subQ33,subQ55,subQ44,subQ31,subQ27,subQ81,subQ23,subQ51,subQ77,subQ21,subQ17,subQ48,subQ59,subQ63,subQ65,subQ69,subQ75,subQ79,subQ94,subQ83,subQ19,subQ85,subQ87,subQ90,subQ92,subQ71,subQ39,subQ96,subQ98,subQ100,subQ73,subQ35,subQ67,subQ25,subQ102,subQ29,subQ104,subQ15,subQ13,subQ11,subQ9,subQ7,subQ5,subQ3])],"derivedFrom":subQ1}),makeQuery(id+"F4.boolean.opBoolean","SPLIT",EDGE,{"disambiguationData":[TD([subQ49,subQ42,subQ61,subQ46,subQ57,subQ108,subQ37,subQ109,subQ53,subQ33,subQ55,subQ44,subQ31,subQ27,subQ81,subQ23,subQ51,subQ77,subQ21,subQ17,subQ48,subQ59,subQ63,subQ65,subQ69,subQ75,subQ79,subQ94,subQ83,subQ19,subQ85,subQ87,subQ90,subQ92,subQ71,subQ39,subQ96,subQ98,subQ100,subQ73,subQ35,subQ67,subQ25,subQ102,subQ29,subQ104,subQ15,subQ13,subQ11,subQ9,subQ7,subQ5,subQ3])],"derivedFrom":subQ1}),makeQuery(id+"F4.boolean.opBoolean","SPLIT",EDGE,{"disambiguationData":[TD([subQ49,subQ42,subQ61,subQ46,subQ57,subQ37,subQ109,subQ53,subQ110,subQ33,subQ55,subQ44,subQ31,subQ27,subQ81,subQ23,subQ51,subQ77,subQ21,subQ17,subQ48,subQ59,subQ63,subQ65,subQ69,subQ75,subQ79,subQ94,subQ83,subQ19,subQ85,subQ87,subQ90,subQ92,subQ71,subQ39,subQ96,subQ98,subQ100,subQ73,subQ35,subQ67,subQ25,subQ102,subQ29,subQ104,subQ15,subQ13,subQ11,subQ9,subQ7,subQ5,subQ3])],"derivedFrom":subQ1}),makeQuery(id+"F4.boolean.opBoolean","SPLIT",EDGE,{"disambiguationData":[TD([subQ49,subQ42,subQ61,subQ46,subQ57,subQ37,subQ53,subQ110,subQ33,subQ111,subQ55,subQ44,subQ31,subQ27,subQ81,subQ23,subQ51,subQ77,subQ21,subQ17,subQ48,subQ59,subQ63,subQ65,subQ69,subQ75,subQ79,subQ94,subQ83,subQ19,subQ85,subQ87,subQ90,subQ92,subQ71,subQ39,subQ96,subQ98,subQ100,subQ73,subQ35,subQ67,subQ25,subQ102,subQ29,subQ104,subQ15,subQ13,subQ11,subQ9,subQ7,subQ5,subQ3])],"derivedFrom":subQ1}),makeQuery(id+"F4.boolean.opBoolean","SPLIT",EDGE,{"disambiguationData":[TD([subQ49,subQ42,subQ61,subQ46,subQ57,subQ37,subQ53,subQ33,subQ111,subQ55,subQ112,subQ44,subQ31,subQ27,subQ81,subQ23,subQ51,subQ77,subQ21,subQ17,subQ48,subQ59,subQ63,subQ65,subQ69,subQ75,subQ79,subQ94,subQ83,subQ19,subQ85,subQ87,subQ90,subQ92,subQ71,subQ39,subQ96,subQ98,subQ100,subQ73,subQ35,subQ67,subQ25,subQ102,subQ29,subQ104,subQ15,subQ13,subQ11,subQ9,subQ7,subQ5,subQ3])],"derivedFrom":subQ1}),makeQuery(id+"F4.boolean.opBoolean","SPLIT",EDGE,{"disambiguationData":[TD([subQ49,subQ42,subQ61,subQ46,subQ57,subQ37,subQ53,subQ33,subQ55,subQ112,subQ44,subQ113,subQ31,subQ27,subQ81,subQ23,subQ51,subQ77,subQ21,subQ17,subQ48,subQ59,subQ63,subQ65,subQ69,subQ75,subQ79,subQ94,subQ83,subQ19,subQ85,subQ87,subQ90,subQ92,subQ71,subQ39,subQ96,subQ98,subQ100,subQ73,subQ35,subQ67,subQ25,subQ102,subQ29,subQ104,subQ15,subQ13,subQ11,subQ9,subQ7,subQ5,subQ3])],"derivedFrom":subQ1}),makeQuery(id+"F4.boolean.opBoolean","SPLIT",EDGE,{"disambiguationData":[TD([subQ49,subQ42,subQ61,subQ46,subQ57,subQ37,subQ53,subQ33,subQ55,subQ44,subQ113,subQ31,subQ114,subQ27,subQ81,subQ23,subQ51,subQ77,subQ21,subQ17,subQ48,subQ59,subQ63,subQ65,subQ69,subQ75,subQ79,subQ94,subQ83,subQ19,subQ85,subQ87,subQ90,subQ92,subQ71,subQ39,subQ96,subQ98,subQ100,subQ73,subQ35,subQ67,subQ25,subQ102,subQ29,subQ104,subQ15,subQ13,subQ11,subQ9,subQ7,subQ5,subQ3])],"derivedFrom":subQ1}),makeQuery(id+"F4.boolean.opBoolean","SPLIT",EDGE,{"disambiguationData":[TD([subQ49,subQ42,subQ61,subQ46,subQ57,subQ37,subQ53,subQ33,subQ55,subQ44,subQ31,subQ114,subQ27,subQ115,subQ81,subQ23,subQ51,subQ77,subQ21,subQ17,subQ48,subQ59,subQ63,subQ65,subQ69,subQ75,subQ79,subQ94,subQ83,subQ19,subQ85,subQ87,subQ90,subQ92,subQ71,subQ39,subQ96,subQ98,subQ100,subQ73,subQ35,subQ67,subQ25,subQ102,subQ29,subQ104,subQ15,subQ13,subQ11,subQ9,subQ7,subQ5,subQ3])],"derivedFrom":subQ1}),makeQuery(id+"F4.boolean.opBoolean","SPLIT",EDGE,{"disambiguationData":[TD([subQ49,subQ42,subQ61,subQ46,subQ57,subQ37,subQ53,subQ33,subQ55,subQ44,subQ31,subQ27,subQ115,subQ81,subQ116,subQ23,subQ51,subQ77,subQ21,subQ17,subQ48,subQ59,subQ63,subQ65,subQ69,subQ75,subQ79,subQ94,subQ83,subQ19,subQ85,subQ87,subQ90,subQ92,subQ71,subQ39,subQ96,subQ98,subQ100,subQ73,subQ35,subQ67,subQ25,subQ102,subQ29,subQ104,subQ15,subQ13,subQ11,subQ9,subQ7,subQ5,subQ3])],"derivedFrom":subQ1}),makeQuery(id+"F4.boolean.opBoolean","SPLIT",EDGE,{"disambiguationData":[TD([subQ49,subQ42,subQ61,subQ46,subQ57,subQ37,subQ53,subQ33,subQ55,subQ44,subQ31,subQ27,subQ81,subQ116,subQ23,subQ117,subQ51,subQ77,subQ21,subQ17,subQ48,subQ59,subQ63,subQ65,subQ69,subQ75,subQ79,subQ94,subQ83,subQ19,subQ85,subQ87,subQ90,subQ92,subQ71,subQ39,subQ96,subQ98,subQ100,subQ73,subQ35,subQ67,subQ25,subQ102,subQ29,subQ104,subQ15,subQ13,subQ11,subQ9,subQ7,subQ5,subQ3])],"derivedFrom":subQ1}),makeQuery(id+"F4.boolean.opBoolean","SPLIT",EDGE,{"disambiguationData":[TD([subQ49,subQ42,subQ61,subQ46,subQ57,subQ37,subQ53,subQ33,subQ55,subQ44,subQ31,subQ27,subQ81,subQ23,subQ117,subQ51,subQ118,subQ77,subQ21,subQ17,subQ48,subQ59,subQ63,subQ65,subQ69,subQ75,subQ79,subQ94,subQ83,subQ19,subQ85,subQ87,subQ90,subQ92,subQ71,subQ39,subQ96,subQ98,subQ100,subQ73,subQ35,subQ67,subQ25,subQ102,subQ29,subQ104,subQ15,subQ13,subQ11,subQ9,subQ7,subQ5,subQ3])],"derivedFrom":subQ1}),makeQuery(id+"F4.boolean.opBoolean","SPLIT",EDGE,{"disambiguationData":[TD([subQ49,subQ42,subQ61,subQ46,subQ57,subQ37,subQ53,subQ33,subQ55,subQ44,subQ31,subQ27,subQ81,subQ23,subQ51,subQ118,subQ77,subQ119,subQ21,subQ17,subQ48,subQ59,subQ63,subQ65,subQ69,subQ75,subQ79,subQ94,subQ83,subQ19,subQ85,subQ87,subQ90,subQ92,subQ71,subQ39,subQ96,subQ98,subQ100,subQ73,subQ35,subQ67,subQ25,subQ102,subQ29,subQ104,subQ15,subQ13,subQ11,subQ9,subQ7,subQ5,subQ3])],"derivedFrom":subQ1}),makeQuery(id+"F4.boolean.opBoolean","SPLIT",EDGE,{"disambiguationData":[TD([subQ49,subQ42,subQ61,subQ46,subQ57,subQ37,subQ53,subQ33,subQ55,subQ44,subQ31,subQ27,subQ81,subQ23,subQ51,subQ77,subQ119,subQ21,subQ120,subQ17,subQ48,subQ59,subQ63,subQ65,subQ69,subQ75,subQ79,subQ94,subQ83,subQ19,subQ85,subQ87,subQ90,subQ92,subQ71,subQ39,subQ96,subQ98,subQ100,subQ73,subQ35,subQ67,subQ25,subQ102,subQ29,subQ104,subQ15,subQ13,subQ11,subQ9,subQ7,subQ5,subQ3])],"derivedFrom":subQ1}),makeQuery(id+"F4.boolean.opBoolean","SPLIT",EDGE,{"disambiguationData":[TD([subQ49,subQ42,subQ61,subQ46,subQ57,subQ37,subQ53,subQ33,subQ55,subQ44,subQ31,subQ27,subQ81,subQ23,subQ51,subQ77,subQ21,subQ120,subQ17,subQ121,subQ48,subQ59,subQ63,subQ65,subQ69,subQ75,subQ79,subQ94,subQ83,subQ19,subQ85,subQ87,subQ90,subQ92,subQ71,subQ39,subQ96,subQ98,subQ100,subQ73,subQ35,subQ67,subQ25,subQ102,subQ29,subQ104,subQ15,subQ13,subQ11,subQ9,subQ7,subQ5,subQ3])],"derivedFrom":subQ1}),makeQuery(id+"F4.boolean.opBoolean","SPLIT",EDGE,{"disambiguationData":[TD([subQ49,subQ42,subQ61,subQ46,subQ57,subQ37,subQ53,subQ33,subQ55,subQ44,subQ31,subQ27,subQ81,subQ23,subQ51,subQ77,subQ21,subQ17,subQ121,subQ48,subQ122,subQ59,subQ63,subQ65,subQ69,subQ75,subQ79,subQ94,subQ83,subQ19,subQ85,subQ87,subQ90,subQ92,subQ71,subQ39,subQ96,subQ98,subQ100,subQ73,subQ35,subQ67,subQ25,subQ102,subQ29,subQ104,subQ15,subQ13,subQ11,subQ9,subQ7,subQ5,subQ3])],"derivedFrom":subQ1}),makeQuery(id+"F4.boolean.opBoolean","SPLIT",EDGE,{"disambiguationData":[TD([subQ49,subQ42,subQ61,subQ46,subQ57,subQ37,subQ53,subQ33,subQ55,subQ44,subQ31,subQ27,subQ81,subQ23,subQ51,subQ77,subQ21,subQ17,subQ48,subQ122,subQ59,subQ123,subQ63,subQ65,subQ69,subQ75,subQ79,subQ94,subQ83,subQ19,subQ85,subQ87,subQ90,subQ92,subQ71,subQ39,subQ96,subQ98,subQ100,subQ73,subQ35,subQ67,subQ25,subQ102,subQ29,subQ104,subQ15,subQ13,subQ11,subQ9,subQ7,subQ5,subQ3])],"derivedFrom":subQ1}),makeQuery(id+"F4.boolean.opBoolean","SPLIT",EDGE,{"disambiguationData":[TD([subQ49,subQ42,subQ61,subQ46,subQ57,subQ37,subQ53,subQ33,subQ55,subQ44,subQ31,subQ27,subQ81,subQ23,subQ51,subQ77,subQ21,subQ17,subQ48,subQ59,subQ123,subQ63,subQ124,subQ65,subQ69,subQ75,subQ79,subQ94,subQ83,subQ19,subQ85,subQ87,subQ90,subQ92,subQ71,subQ39,subQ96,subQ98,subQ100,subQ73,subQ35,subQ67,subQ25,subQ102,subQ29,subQ104,subQ15,subQ13,subQ11,subQ9,subQ7,subQ5,subQ3])],"derivedFrom":subQ1}),makeQuery(id+"F4.boolean.opBoolean","SPLIT",EDGE,{"disambiguationData":[TD([subQ49,subQ42,subQ61,subQ46,subQ57,subQ37,subQ53,subQ33,subQ55,subQ44,subQ31,subQ27,subQ81,subQ23,subQ51,subQ77,subQ21,subQ17,subQ48,subQ59,subQ63,subQ124,subQ65,subQ125,subQ69,subQ75,subQ79,subQ94,subQ83,subQ19,subQ85,subQ87,subQ90,subQ92,subQ71,subQ39,subQ96,subQ98,subQ100,subQ73,subQ35,subQ67,subQ25,subQ102,subQ29,subQ104,subQ15,subQ13,subQ11,subQ9,subQ7,subQ5,subQ3])],"derivedFrom":subQ1}),makeQuery(id+"F4.boolean.opBoolean","SPLIT",EDGE,{"disambiguationData":[TD([subQ49,subQ42,subQ61,subQ46,subQ57,subQ37,subQ53,subQ33,subQ55,subQ44,subQ31,subQ27,subQ81,subQ23,subQ51,subQ77,subQ21,subQ17,subQ48,subQ59,subQ63,subQ65,subQ125,subQ69,subQ126,subQ75,subQ79,subQ94,subQ83,subQ19,subQ85,subQ87,subQ90,subQ92,subQ71,subQ39,subQ96,subQ98,subQ100,subQ73,subQ35,subQ67,subQ25,subQ102,subQ29,subQ104,subQ15,subQ13,subQ11,subQ9,subQ7,subQ5,subQ3])],"derivedFrom":subQ1}),makeQuery(id+"F4.boolean.opBoolean","SPLIT",EDGE,{"disambiguationData":[TD([subQ49,subQ42,subQ61,subQ46,subQ57,subQ37,subQ53,subQ33,subQ55,subQ44,subQ31,subQ27,subQ81,subQ23,subQ51,subQ77,subQ21,subQ17,subQ48,subQ59,subQ63,subQ65,subQ69,subQ126,subQ75,subQ127,subQ79,subQ94,subQ83,subQ19,subQ85,subQ87,subQ90,subQ92,subQ71,subQ39,subQ96,subQ98,subQ100,subQ73,subQ35,subQ67,subQ25,subQ102,subQ29,subQ104,subQ15,subQ13,subQ11,subQ9,subQ7,subQ5,subQ3])],"derivedFrom":subQ1}),makeQuery(id+"F4.boolean.opBoolean","SPLIT",EDGE,{"disambiguationData":[TD([subQ49,subQ42,subQ61,subQ46,subQ57,subQ37,subQ53,subQ33,subQ55,subQ44,subQ31,subQ27,subQ81,subQ23,subQ51,subQ77,subQ21,subQ17,subQ48,subQ59,subQ63,subQ65,subQ69,subQ75,subQ127,subQ79,subQ128,subQ94,subQ83,subQ19,subQ85,subQ87,subQ90,subQ92,subQ71,subQ39,subQ96,subQ98,subQ100,subQ73,subQ35,subQ67,subQ25,subQ102,subQ29,subQ104,subQ15,subQ13,subQ11,subQ9,subQ7,subQ5,subQ3])],"derivedFrom":subQ1}),makeQuery(id+"F4.boolean.opBoolean","SPLIT",EDGE,{"disambiguationData":[TD([subQ49,subQ42,subQ61,subQ46,subQ57,subQ37,subQ53,subQ33,subQ55,subQ44,subQ31,subQ27,subQ81,subQ23,subQ51,subQ77,subQ21,subQ17,subQ48,subQ59,subQ63,subQ65,subQ69,subQ75,subQ79,subQ128,subQ94,subQ129,subQ83,subQ19,subQ85,subQ87,subQ90,subQ92,subQ71,subQ39,subQ96,subQ98,subQ100,subQ73,subQ35,subQ67,subQ25,subQ102,subQ29,subQ104,subQ15,subQ13,subQ11,subQ9,subQ7,subQ5,subQ3])],"derivedFrom":subQ1}),makeQuery(id+"F4.boolean.opBoolean","SPLIT",EDGE,{"disambiguationData":[TD([subQ49,subQ42,subQ61,subQ46,subQ57,subQ37,subQ53,subQ33,subQ55,subQ44,subQ31,subQ27,subQ81,subQ23,subQ51,subQ77,subQ21,subQ17,subQ48,subQ59,subQ63,subQ65,subQ69,subQ75,subQ79,subQ94,subQ129,subQ83,subQ130,subQ19,subQ85,subQ87,subQ90,subQ92,subQ71,subQ39,subQ96,subQ98,subQ100,subQ73,subQ35,subQ67,subQ25,subQ102,subQ29,subQ104,subQ15,subQ13,subQ11,subQ9,subQ7,subQ5,subQ3])],"derivedFrom":subQ1}),makeQuery(id+"F4.boolean.opBoolean","SPLIT",EDGE,{"disambiguationData":[TD([subQ49,subQ42,subQ61,subQ46,subQ57,subQ37,subQ53,subQ33,subQ55,subQ44,subQ31,subQ27,subQ81,subQ23,subQ51,subQ77,subQ21,subQ17,subQ48,subQ59,subQ63,subQ65,subQ69,subQ75,subQ79,subQ94,subQ83,subQ130,subQ19,subQ131,subQ85,subQ87,subQ90,subQ92,subQ71,subQ39,subQ96,subQ98,subQ100,subQ73,subQ35,subQ67,subQ25,subQ102,subQ29,subQ104,subQ15,subQ13,subQ11,subQ9,subQ7,subQ5,subQ3])],"derivedFrom":subQ1}),makeQuery(id+"F4.boolean.opBoolean","SPLIT",EDGE,{"disambiguationData":[TD([subQ49,subQ42,subQ61,subQ46,subQ57,subQ37,subQ53,subQ33,subQ55,subQ44,subQ31,subQ27,subQ81,subQ23,subQ51,subQ77,subQ21,subQ17,subQ48,subQ59,subQ63,subQ65,subQ69,subQ75,subQ79,subQ94,subQ83,subQ19,subQ131,subQ85,subQ132,subQ87,subQ90,subQ92,subQ71,subQ39,subQ96,subQ98,subQ100,subQ73,subQ35,subQ67,subQ25,subQ102,subQ29,subQ104,subQ15,subQ13,subQ11,subQ9,subQ7,subQ5,subQ3])],"derivedFrom":subQ1}),makeQuery(id+"F4.boolean.opBoolean","SPLIT",EDGE,{"disambiguationData":[TD([subQ49,subQ42,subQ61,subQ46,subQ57,subQ37,subQ53,subQ33,subQ55,subQ44,subQ31,subQ27,subQ81,subQ23,subQ51,subQ77,subQ21,subQ17,subQ48,subQ59,subQ63,subQ65,subQ69,subQ75,subQ79,subQ94,subQ83,subQ19,subQ85,subQ132,subQ87,subQ133,subQ90,subQ92,subQ71,subQ39,subQ96,subQ98,subQ100,subQ73,subQ35,subQ67,subQ25,subQ102,subQ29,subQ104,subQ15,subQ13,subQ11,subQ9,subQ7,subQ5,subQ3])],"derivedFrom":subQ1}),makeQuery(id+"F4.boolean.opBoolean","SPLIT",EDGE,{"disambiguationData":[TD([subQ49,subQ42,subQ61,subQ46,subQ57,subQ37,subQ53,subQ33,subQ55,subQ44,subQ31,subQ27,subQ81,subQ23,subQ51,subQ77,subQ21,subQ17,subQ48,subQ59,subQ63,subQ65,subQ69,subQ75,subQ79,subQ94,subQ83,subQ19,subQ85,subQ87,subQ133,subQ90,subQ134,subQ92,subQ71,subQ39,subQ96,subQ98,subQ100,subQ73,subQ35,subQ67,subQ25,subQ102,subQ29,subQ104,subQ15,subQ13,subQ11,subQ9,subQ7,subQ5,subQ3])],"derivedFrom":subQ1}),makeQuery(id+"F4.boolean.opBoolean","SPLIT",EDGE,{"disambiguationData":[TD([subQ49,subQ42,subQ61,subQ46,subQ57,subQ37,subQ53,subQ33,subQ55,subQ44,subQ31,subQ27,subQ81,subQ23,subQ51,subQ77,subQ21,subQ17,subQ48,subQ59,subQ63,subQ65,subQ69,subQ75,subQ79,subQ94,subQ83,subQ19,subQ85,subQ87,subQ90,subQ134,subQ92,subQ135,subQ71,subQ39,subQ96,subQ98,subQ100,subQ73,subQ35,subQ67,subQ25,subQ102,subQ29,subQ104,subQ15,subQ13,subQ11,subQ9,subQ7,subQ5,subQ3])],"derivedFrom":subQ1}),makeQuery(id+"F4.boolean.opBoolean","SPLIT",EDGE,{"disambiguationData":[TD([subQ49,subQ42,subQ61,subQ46,subQ57,subQ37,subQ53,subQ33,subQ55,subQ44,subQ31,subQ27,subQ81,subQ23,subQ51,subQ77,subQ21,subQ17,subQ48,subQ59,subQ63,subQ65,subQ69,subQ75,subQ79,subQ94,subQ83,subQ19,subQ85,subQ87,subQ90,subQ92,subQ135,subQ71,subQ136,subQ39,subQ96,subQ98,subQ100,subQ73,subQ35,subQ67,subQ25,subQ102,subQ29,subQ104,subQ15,subQ13,subQ11,subQ9,subQ7,subQ5,subQ3])],"derivedFrom":subQ1}),makeQuery(id+"F4.boolean.opBoolean","SPLIT",EDGE,{"disambiguationData":[TD([subQ49,subQ42,subQ61,subQ46,subQ57,subQ37,subQ53,subQ33,subQ55,subQ44,subQ31,subQ27,subQ81,subQ23,subQ51,subQ77,subQ21,subQ17,subQ48,subQ59,subQ63,subQ65,subQ69,subQ75,subQ79,subQ94,subQ83,subQ19,subQ85,subQ87,subQ90,subQ92,subQ71,subQ136,subQ39,subQ137,subQ96,subQ98,subQ100,subQ73,subQ35,subQ67,subQ25,subQ102,subQ29,subQ104,subQ15,subQ13,subQ11,subQ9,subQ7,subQ5,subQ3])],"derivedFrom":subQ1}),makeQuery(id+"F4.boolean.opBoolean","SPLIT",EDGE,{"disambiguationData":[TD([subQ49,subQ42,subQ61,subQ46,subQ57,subQ37,subQ53,subQ33,subQ55,subQ44,subQ31,subQ27,subQ81,subQ23,subQ51,subQ77,subQ21,subQ17,subQ48,subQ59,subQ63,subQ65,subQ69,subQ75,subQ79,subQ94,subQ83,subQ19,subQ85,subQ87,subQ90,subQ92,subQ71,subQ39,subQ137,subQ96,subQ138,subQ98,subQ100,subQ73,subQ35,subQ67,subQ25,subQ102,subQ29,subQ104,subQ15,subQ13,subQ11,subQ9,subQ7,subQ5,subQ3])],"derivedFrom":subQ1}),makeQuery(id+"F4.boolean.opBoolean","SPLIT",EDGE,{"disambiguationData":[TD([subQ49,subQ42,subQ61,subQ46,subQ57,subQ37,subQ53,subQ33,subQ55,subQ44,subQ31,subQ27,subQ81,subQ23,subQ51,subQ77,subQ21,subQ17,subQ48,subQ59,subQ63,subQ65,subQ69,subQ75,subQ79,subQ94,subQ83,subQ19,subQ85,subQ87,subQ90,subQ92,subQ71,subQ39,subQ96,subQ138,subQ98,subQ139,subQ100,subQ73,subQ35,subQ67,subQ25,subQ102,subQ29,subQ104,subQ15,subQ13,subQ11,subQ9,subQ7,subQ5,subQ3])],"derivedFrom":subQ1}),makeQuery(id+"F4.boolean.opBoolean","SPLIT",EDGE,{"disambiguationData":[TD([subQ49,subQ42,subQ61,subQ46,subQ57,subQ37,subQ53,subQ33,subQ55,subQ44,subQ31,subQ27,subQ81,subQ23,subQ51,subQ77,subQ21,subQ17,subQ48,subQ59,subQ63,subQ65,subQ69,subQ75,subQ79,subQ94,subQ83,subQ19,subQ85,subQ87,subQ90,subQ92,subQ71,subQ39,subQ96,subQ98,subQ139,subQ100,subQ140,subQ73,subQ35,subQ67,subQ25,subQ102,subQ29,subQ104,subQ15,subQ13,subQ11,subQ9,subQ7,subQ5,subQ3])],"derivedFrom":subQ1}),makeQuery(id+"F4.boolean.opBoolean","SPLIT",EDGE,{"disambiguationData":[TD([subQ49,subQ42,subQ61,subQ46,subQ57,subQ37,subQ53,subQ33,subQ55,subQ44,subQ31,subQ27,subQ81,subQ23,subQ51,subQ77,subQ21,subQ17,subQ48,subQ59,subQ63,subQ65,subQ69,subQ75,subQ79,subQ94,subQ83,subQ19,subQ85,subQ87,subQ90,subQ92,subQ71,subQ39,subQ96,subQ98,subQ100,subQ140,subQ73,subQ141,subQ35,subQ67,subQ25,subQ102,subQ29,subQ104,subQ15,subQ13,subQ11,subQ9,subQ7,subQ5,subQ3])],"derivedFrom":subQ1}),makeQuery(id+"F4.boolean.opBoolean","SPLIT",EDGE,{"disambiguationData":[TD([subQ49,subQ42,subQ61,subQ46,subQ57,subQ37,subQ53,subQ33,subQ55,subQ44,subQ31,subQ27,subQ81,subQ23,subQ51,subQ77,subQ21,subQ17,subQ48,subQ59,subQ63,subQ65,subQ69,subQ75,subQ79,subQ94,subQ83,subQ19,subQ85,subQ87,subQ90,subQ92,subQ71,subQ39,subQ96,subQ98,subQ100,subQ73,subQ141,subQ35,subQ142,subQ67,subQ25,subQ102,subQ29,subQ104,subQ15,subQ13,subQ11,subQ9,subQ7,subQ5,subQ3])],"derivedFrom":subQ1}),makeQuery(id+"F4.boolean.opBoolean","SPLIT",EDGE,{"disambiguationData":[TD([subQ49,subQ42,subQ61,subQ46,subQ57,subQ37,subQ53,subQ33,subQ55,subQ44,subQ31,subQ27,subQ81,subQ23,subQ51,subQ77,subQ21,subQ17,subQ48,subQ59,subQ63,subQ65,subQ69,subQ75,subQ79,subQ94,subQ83,subQ19,subQ85,subQ87,subQ90,subQ92,subQ71,subQ39,subQ96,subQ98,subQ100,subQ73,subQ35,subQ142,subQ67,subQ143,subQ25,subQ102,subQ29,subQ104,subQ15,subQ13,subQ11,subQ9,subQ7,subQ5,subQ3])],"derivedFrom":subQ1}),makeQuery(id+"F4.boolean.opBoolean","SPLIT",EDGE,{"disambiguationData":[TD([subQ49,subQ42,subQ61,subQ46,subQ57,subQ37,subQ53,subQ33,subQ55,subQ44,subQ31,subQ27,subQ81,subQ23,subQ51,subQ77,subQ21,subQ17,subQ48,subQ59,subQ63,subQ65,subQ69,subQ75,subQ79,subQ94,subQ83,subQ19,subQ85,subQ87,subQ90,subQ92,subQ71,subQ39,subQ96,subQ98,subQ100,subQ73,subQ35,subQ67,subQ143,subQ25,subQ144,subQ102,subQ29,subQ104,subQ15,subQ13,subQ11,subQ9,subQ7,subQ5,subQ3])],"derivedFrom":subQ1}),makeQuery(id+"F4.boolean.opBoolean","SPLIT",EDGE,{"disambiguationData":[TD([subQ49,subQ42,subQ61,subQ46,subQ57,subQ37,subQ53,subQ33,subQ55,subQ44,subQ31,subQ27,subQ81,subQ23,subQ51,subQ77,subQ21,subQ17,subQ48,subQ59,subQ63,subQ65,subQ69,subQ75,subQ79,subQ94,subQ83,subQ19,subQ85,subQ87,subQ90,subQ92,subQ71,subQ39,subQ96,subQ98,subQ100,subQ73,subQ35,subQ67,subQ25,subQ144,subQ102,subQ145,subQ29,subQ104,subQ15,subQ13,subQ11,subQ9,subQ7,subQ5,subQ3])],"derivedFrom":subQ1}),makeQuery(id+"F4.boolean.opBoolean","SPLIT",EDGE,{"disambiguationData":[TD([subQ49,subQ42,subQ61,subQ46,subQ57,subQ37,subQ53,subQ33,subQ55,subQ44,subQ31,subQ27,subQ81,subQ23,subQ51,subQ77,subQ21,subQ17,subQ48,subQ59,subQ63,subQ65,subQ69,subQ75,subQ79,subQ94,subQ83,subQ19,subQ85,subQ87,subQ90,subQ92,subQ71,subQ39,subQ96,subQ98,subQ100,subQ73,subQ35,subQ67,subQ25,subQ102,subQ145,subQ29,subQ146,subQ104,subQ15,subQ13,subQ11,subQ9,subQ7,subQ5,subQ3])],"derivedFrom":subQ1}),makeQuery(id+"F4.boolean.opBoolean","SPLIT",EDGE,{"disambiguationData":[TD([subQ49,subQ42,subQ61,subQ46,subQ57,subQ37,subQ53,subQ33,subQ55,subQ44,subQ31,subQ27,subQ81,subQ23,subQ51,subQ77,subQ21,subQ17,subQ48,subQ59,subQ63,subQ65,subQ69,subQ75,subQ79,subQ94,subQ83,subQ19,subQ85,subQ87,subQ90,subQ92,subQ71,subQ39,subQ96,subQ98,subQ100,subQ73,subQ35,subQ67,subQ25,subQ102,subQ29,subQ146,subQ104,subQ147,subQ15,subQ13,subQ11,subQ9,subQ7,subQ5,subQ3])],"derivedFrom":subQ1}),makeQuery(id+"F4.boolean.opBoolean","SPLIT",EDGE,{"disambiguationData":[TD([subQ49,subQ42,subQ61,subQ46,subQ57,subQ37,subQ53,subQ33,subQ55,subQ44,subQ31,subQ27,subQ81,subQ23,subQ51,subQ77,subQ21,subQ17,subQ48,subQ59,subQ63,subQ65,subQ69,subQ75,subQ79,subQ94,subQ83,subQ19,subQ85,subQ87,subQ90,subQ92,subQ71,subQ39,subQ96,subQ98,subQ100,subQ73,subQ35,subQ67,subQ25,subQ102,subQ29,subQ104,subQ147,subQ15,subQ148,subQ13,subQ11,subQ9,subQ7,subQ5,subQ3])],"derivedFrom":subQ1}),makeQuery(id+"F4.boolean.opBoolean","SPLIT",EDGE,{"disambiguationData":[TD([subQ49,subQ42,subQ61,subQ46,subQ57,subQ37,subQ53,subQ33,subQ55,subQ44,subQ31,subQ27,subQ81,subQ23,subQ51,subQ77,subQ21,subQ17,subQ48,subQ59,subQ63,subQ65,subQ69,subQ75,subQ79,subQ94,subQ83,subQ19,subQ85,subQ87,subQ90,subQ92,subQ71,subQ39,subQ96,subQ98,subQ100,subQ73,subQ35,subQ67,subQ25,subQ102,subQ29,subQ104,subQ15,subQ148,subQ13,subQ149,subQ11,subQ9,subQ7,subQ5,subQ3])],"derivedFrom":subQ1}),makeQuery(id+"F4.boolean.opBoolean","SPLIT",EDGE,{"disambiguationData":[TD([subQ49,subQ42,subQ61,subQ46,subQ57,subQ37,subQ53,subQ33,subQ55,subQ44,subQ31,subQ27,subQ81,subQ23,subQ51,subQ77,subQ21,subQ17,subQ48,subQ59,subQ63,subQ65,subQ69,subQ75,subQ79,subQ94,subQ83,subQ19,subQ85,subQ87,subQ90,subQ92,subQ71,subQ39,subQ96,subQ98,subQ100,subQ73,subQ35,subQ67,subQ25,subQ102,subQ29,subQ104,subQ15,subQ13,subQ149,subQ11,subQ150,subQ9,subQ7,subQ5,subQ3])],"derivedFrom":subQ1}),makeQuery(id+"F4.boolean.opBoolean","SPLIT",EDGE,{"disambiguationData":[TD([subQ49,subQ42,subQ61,subQ46,subQ57,subQ37,subQ53,subQ33,subQ55,subQ44,subQ31,subQ27,subQ81,subQ23,subQ51,subQ77,subQ21,subQ17,subQ48,subQ59,subQ63,subQ65,subQ69,subQ75,subQ79,subQ94,subQ83,subQ19,subQ85,subQ87,subQ90,subQ92,subQ71,subQ39,subQ96,subQ98,subQ100,subQ73,subQ35,subQ67,subQ25,subQ102,subQ29,subQ104,subQ15,subQ13,subQ11,subQ150,subQ9,subQ151,subQ7,subQ5,subQ3])],"derivedFrom":subQ1}),makeQuery(id+"F4.boolean.opBoolean","SPLIT",EDGE,{"disambiguationData":[TD([subQ49,subQ42,subQ61,subQ46,subQ57,subQ37,subQ53,subQ33,subQ55,subQ44,subQ31,subQ27,subQ81,subQ23,subQ51,subQ77,subQ21,subQ17,subQ48,subQ59,subQ63,subQ65,subQ69,subQ75,subQ79,subQ94,subQ83,subQ19,subQ85,subQ87,subQ90,subQ92,subQ71,subQ39,subQ96,subQ98,subQ100,subQ73,subQ35,subQ67,subQ25,subQ102,subQ29,subQ104,subQ15,subQ13,subQ11,subQ9,subQ151,subQ7,subQ152,subQ5,subQ3])],"derivedFrom":subQ1}),makeQuery(id+"F4.boolean.opBoolean","SPLIT",EDGE,{"disambiguationData":[TD([subQ49,subQ42,subQ61,subQ46,subQ57,subQ37,subQ53,subQ33,subQ55,subQ44,subQ31,subQ27,subQ81,subQ23,subQ51,subQ77,subQ21,subQ17,subQ48,subQ59,subQ63,subQ65,subQ69,subQ75,subQ79,subQ94,subQ83,subQ19,subQ85,subQ87,subQ90,subQ92,subQ71,subQ39,subQ96,subQ98,subQ100,subQ73,subQ35,subQ67,subQ25,subQ102,subQ29,subQ104,subQ15,subQ13,subQ11,subQ9,subQ7,subQ152,subQ5,subQ105,subQ3])],"derivedFrom":subQ1}),makeQuery(id+"F8.opExtrude","CAP_EDGE",EDGE,{"disambiguationData":[OSD([sQuery(id+"F7.wireOp",EDGE,"E14")])],"isStart":true})]});}
            fillet(context, id + "F9", {"entities" : qUnion([Q0]), "radius" : 0.64 * mm, "tangentPropagation" : true, "allowEdgeOverflow" : false});
        }
        {
            var Q0;
            Q0=makeQuery(id+"F1.opExtrude","SWEPT_FACE",FACE,{"disambiguationData":[OSD([sQuery(id+"F0.wireOp",EDGE,"E2.rect.right")])]});
            var sketch = newSketch(context, id + "F10", { "sketchPlane" : qUnion([Q0])});
            skLineSegment(sketch, "E15.bottom", {"start": v(16.41, 17.46) * mm, "end": v(18.12, 17.46) * mm});
            skLineSegment(sketch, "E15.left", {"start": v(16.41, 17.46) * mm, "end": v(16.41, 16.2) * mm});
            skLineSegment(sketch, "E15.right", {"start": v(18.12, 17.46) * mm, "end": v(18.12, 14.49) * mm});
            skLineSegment(sketch, "E16", {"start": v(18.12, 14.49) * mm, "end": v(16.41, 16.2) * mm});
            skSolve(sketch);
        }
        {
            var Q0;
            Q0=makeQuery(id+"F10.imprint","IMPRINT",FACE,{"disambiguationData":[TD([[makeQuery(id+"F10.imprint","IMPRINT",EDGE,{"derivedFrom":sQuery(id+"F10.wireOp",EDGE,"E15.bottom")}),1.0]])]});
            extrude(context, id + "F11", {"entities" : qUnion([Q0]), "operationType" : NewBodyOperationType.REMOVE, "oppositeDirection" : true, "depth" : 25.4 * mm});
        }
    });
